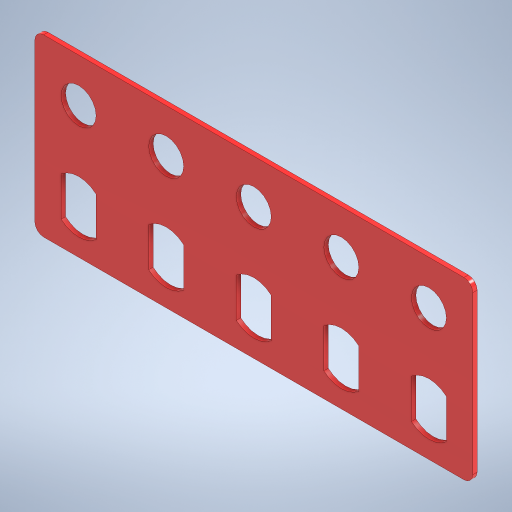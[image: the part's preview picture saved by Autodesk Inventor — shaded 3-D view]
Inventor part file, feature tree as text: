
AUTODESK INVENTOR PART (.ipt)
format: ipt  version: 2024 (Build 280153000, 153)  size: 293,888 bytes
history: native  units: mm
features: extrude x3, fillet x3, sketch x3, pattern_linear x2, other x1
ambient origin geometry x8: Origin, YZ Plane, XZ Plane, XY Plane, X Axis, Y Axis, Z Axis, Center Point
bodies: Body1 (feature_tree)
feature tree (12):
  other  "Těleso1"
  extrude  "Vysunutí1"  Depth=20.0mm
  extrude  "Vysunutí2"  Depth=50.0mm
  pattern_linear  "Obdélníkové pole1"  Spacing1=10.0mm  [1 undecoded]
  fillet  "Zaoblení1"  Radius=10.0mm
  fillet  "Zaoblení2"  Radius=0.5mm
  fillet  "Zaoblení3"  Radius=4.0mm
  extrude  "Vysunutí3"  Depth=5.0mm
  pattern_linear  "Obdélníkové pole2"  Spacing1=5.0mm  [1 undecoded]
  sketch  "Náčrt1"
  sketch  "Náčrt2"
  sketch  "Náčrt3"
note: 2 required parameter values undecoded (feature->parameter linkage not recoverable at this tier; creation-order binding heuristic only, values carry confidence <= 0.55)
